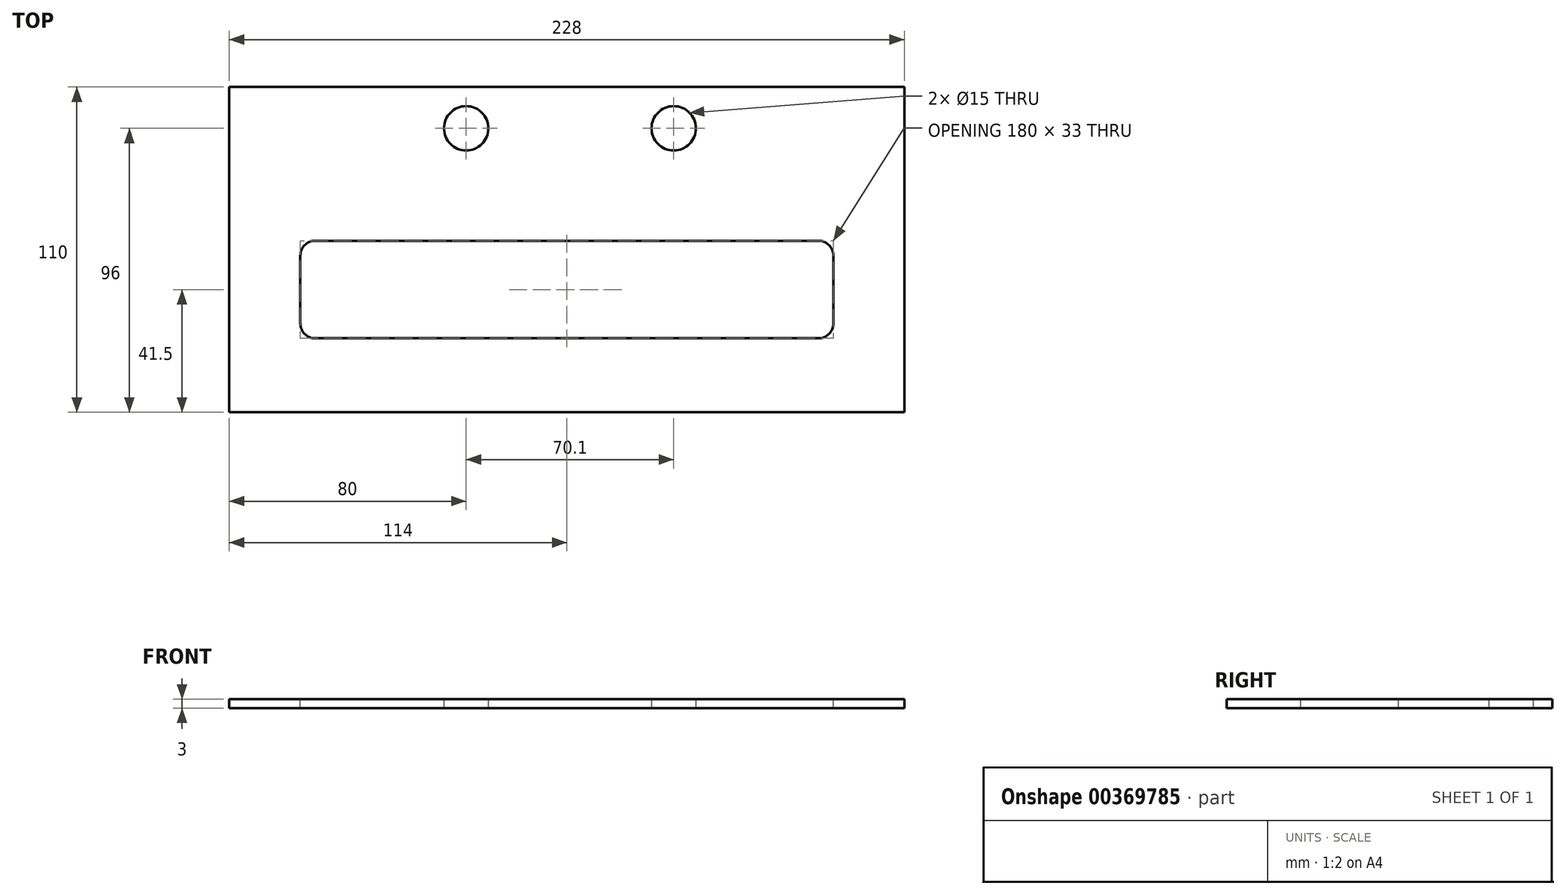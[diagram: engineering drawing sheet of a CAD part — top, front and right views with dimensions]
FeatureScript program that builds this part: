
annotation { "Feature Type Name" : "Feature", "Feature Type Description" : "" }
export const myFeature = defineFeature(function(context is Context, id is Id, definition is map)
    precondition{}
    {
        {
            var Q0;
            Q0=qCreatedBy(makeId("Top.planeOp"),FACE);
            var sketch = newSketch(context, id + "F0", { "sketchPlane" : qUnion([Q0])});
            skLineSegment(sketch, "E0.bottom", {"start": v(0, 0) * mm, "end": v(-228, 0) * mm});
            skLineSegment(sketch, "E0.top", {"start": v(0, 110) * mm, "end": v(-228, 110) * mm});
            skLineSegment(sketch, "E0.left", {"start": v(0, 0) * mm, "end": v(0, 110) * mm});
            skLineSegment(sketch, "E0.right", {"start": v(-228, 0) * mm, "end": v(-228, 110) * mm});
            skSolve(sketch);
        }
        {
            var Q0;
            Q0=makeQuery(id+"F0.imprint","IMPRINT",FACE,{"disambiguationData":[TD([[makeQuery(id+"F0.imprint","IMPRINT",EDGE,{"derivedFrom":sQuery(id+"F0.wireOp",EDGE,"E0.bottom")}),-1.0]])]});
            extrude(context, id + "F1", {"entities" : qUnion([Q0]), "depth" : 3 * mm});
        }
        {
            var Q0;
            Q0=makeQuery(id+"F1.opExtrude","CAP_FACE",FACE,{"disambiguationData":[OSD([sQuery(id+"F0.wireOp",EDGE,"E0.bottom"),sQuery(id+"F0.wireOp",EDGE,"E0.top"),sQuery(id+"F0.wireOp",EDGE,"E0.left"),sQuery(id+"F0.wireOp",EDGE,"E0.right")])],"isStart":false});
            var sketch = newSketch(context, id + "F2", { "sketchPlane" : qUnion([Q0])});
            skLineSegment(sketch, "E1.bottom", {"start": v(-204, 58) * mm, "end": v(-24, 58) * mm});
            skLineSegment(sketch, "E1.top", {"start": v(-204, 25) * mm, "end": v(-24, 25) * mm});
            skLineSegment(sketch, "E1.left", {"start": v(-204, 58) * mm, "end": v(-204, 25) * mm});
            skLineSegment(sketch, "E1.right", {"start": v(-24, 58) * mm, "end": v(-24, 25) * mm});
            skSolve(sketch);
        }
        {
            var Q0;
            Q0=makeQuery(id+"F2.imprint","IMPRINT",FACE,{"disambiguationData":[TD([[makeQuery(id+"F2.imprint","IMPRINT",EDGE,{"derivedFrom":sQuery(id+"F2.wireOp",EDGE,"E1.bottom")}),-1.0]])]});
            extrude(context, id + "F3", {"entities" : qUnion([Q0]), "operationType" : NewBodyOperationType.REMOVE, "oppositeDirection" : true, "depth" : 25 * mm});
        }
        {
            var Q0;
            Q0=makeQuery(id+"F3.boolean.opBoolean","COPY",EDGE,{"derivedFrom":makeQuery(id+"F3.opExtrude","SWEPT_EDGE",EDGE,{"disambiguationData":[OSD([sQuery(id+"F2.wireOp",EDGE,"E1.top"),sQuery(id+"F2.wireOp",EDGE,"E1.right")])]})});
            var Q1;
            Q1=makeQuery(id+"F3.boolean.opBoolean","COPY",EDGE,{"derivedFrom":makeQuery(id+"F3.opExtrude","SWEPT_EDGE",EDGE,{"disambiguationData":[OSD([sQuery(id+"F2.wireOp",EDGE,"E1.bottom"),sQuery(id+"F2.wireOp",EDGE,"E1.right")])]})});
            var Q2;
            Q2=makeQuery(id+"F3.boolean.opBoolean","COPY",EDGE,{"derivedFrom":makeQuery(id+"F3.opExtrude","SWEPT_EDGE",EDGE,{"disambiguationData":[OSD([sQuery(id+"F2.wireOp",EDGE,"E1.bottom"),sQuery(id+"F2.wireOp",EDGE,"E1.left")])]})});
            var Q3;
            Q3=makeQuery(id+"F3.boolean.opBoolean","COPY",EDGE,{"derivedFrom":makeQuery(id+"F3.opExtrude","SWEPT_EDGE",EDGE,{"disambiguationData":[OSD([sQuery(id+"F2.wireOp",EDGE,"E1.top"),sQuery(id+"F2.wireOp",EDGE,"E1.left")])]})});
            fillet(context, id + "F4", {"entities" : qUnion([Q0, Q1, Q2, Q3]), "radius" : 5 * mm, "tangentPropagation" : true, "allowEdgeOverflow" : false});
        }
        {
            var Q0;
            Q0=makeQuery(id+"F1.opExtrude","CAP_FACE",FACE,{"disambiguationData":[OSD([sQuery(id+"F0.wireOp",EDGE,"E0.bottom"),sQuery(id+"F0.wireOp",EDGE,"E0.top"),sQuery(id+"F0.wireOp",EDGE,"E0.left"),sQuery(id+"F0.wireOp",EDGE,"E0.right")])],"isStart":true});
            var sketch = newSketch(context, id + "F5", { "sketchPlane" : qUnion([Q0])});
            skCircle(sketch, "E2", {"center": v(-148, -96) * mm, "radius": 7.5 * mm});
            skCircle(sketch, "E3", {"center": v(-77.9, -96) * mm, "radius": 7.5 * mm});
            skSolve(sketch);
        }
        {
            var Q0;
            Q0 = qSketchRegion(id + "F5", true);
            extrude(context, id + "F6", {"entities" : qUnion([Q0]), "operationType" : NewBodyOperationType.REMOVE, "oppositeDirection" : true, "depth" : 25 * mm});
        }
    });
